# Revit family: Sanitary_Showers_hansgrohe_24588DZR-Raindance-Alive-S-Puro-Showerpipe-300-1jet-with-Ecostat-Element-DZR_NEW01
name_source: partatom
category: Plumbing Fixtures
units: mm (PartAtom-declared; Revit-internal decimal feet)

## family parameters
Always vertical = No
Cut with Voids When Loaded = No
Maintain Annotation Orientation = No
OmniClass Number = 23.31.17.00
OmniClass Title = Showers
Part Type = Normal
Room Calculation Point = No
Round Connector Dimension = Use Diameter
Shared = No
Work Plane-Based = Yes

## types (3) — shared parameters
Connector Description = Water Inlet 12.7mm
Default Elevation = 1219 mm
Description = Raindance Alive S Puro Showerpipe 300 1jet with Ecostat Element DZR
Diameter = 13 mm  [stored 0.0426509 ft]
Manufacturer = Hansgrohe
Material 2 = Hansgrohe - Plastic - Graphite
Model = 24588DZR
Product Page URL = https://www.hansgrohe.com
Product data url = https://bimobject.com
URL = https://www.hansgrohe.com
Version = 1

## per-type parameters (varying)
| type | Material 1 |
| 000 Chrome | Hansgrohe - Metal - 000 Chrome |
| 140 Brushed Bronze | Hansgrohe - Metal - 140 Brushed Bronze |
| 670 Matte Black | Hansgrohe - Metal - 670 Matte Black |

note: [stored X ft] marks values corroborated as IEEE doubles in the binary element streams (Revit-internal decimal feet)

## geometry (parser evidence)
native form markers: Sweep x1
no freeform markers — native parametric forms only
